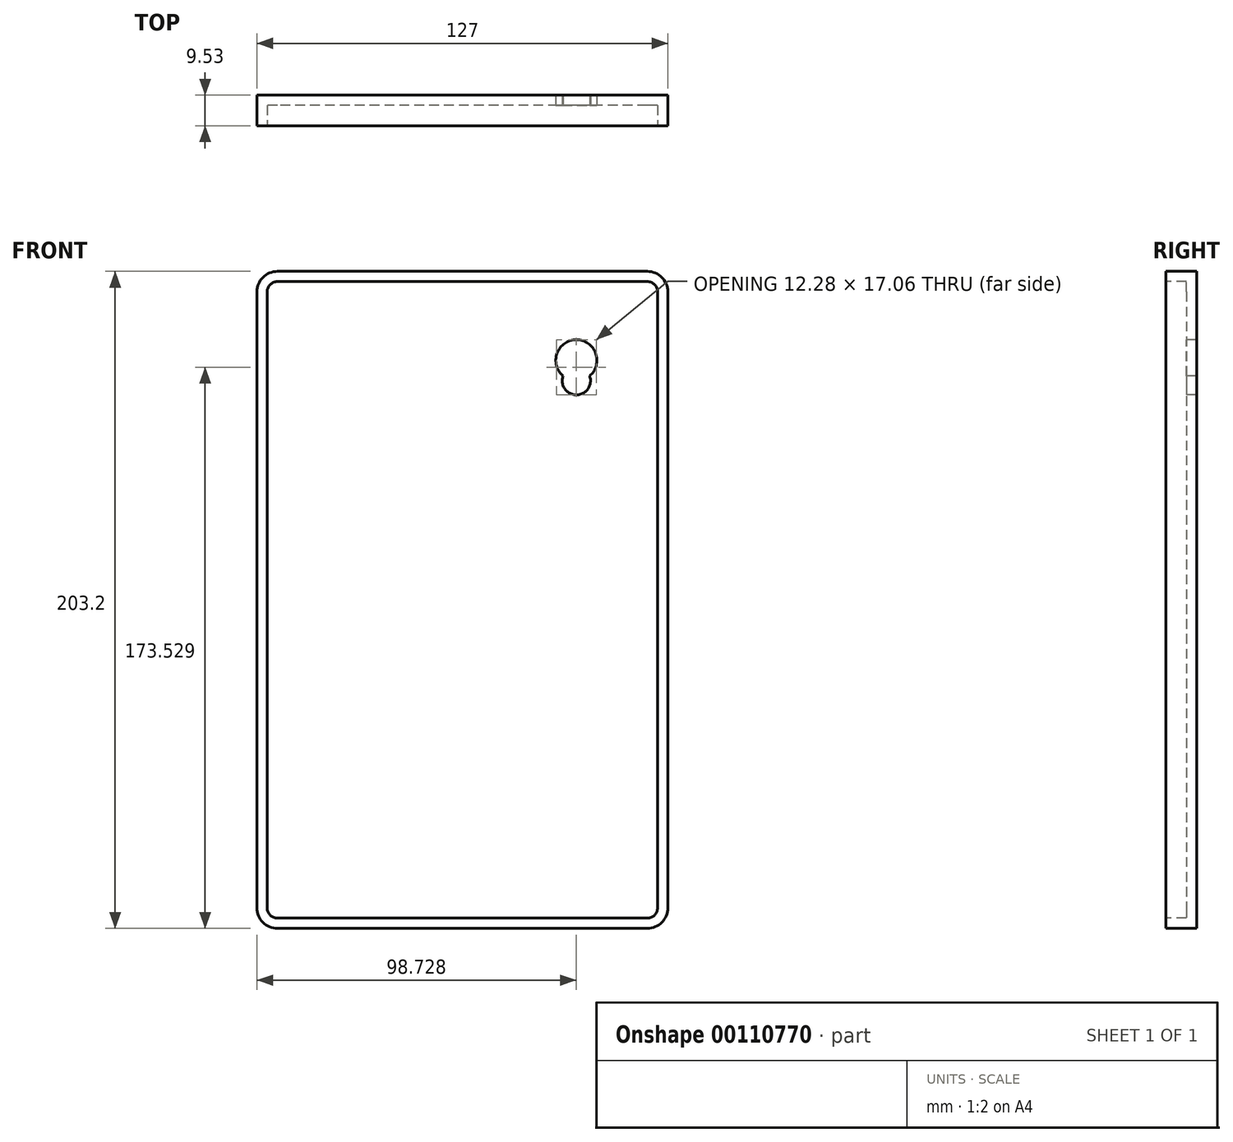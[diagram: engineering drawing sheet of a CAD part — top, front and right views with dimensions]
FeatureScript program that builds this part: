
annotation { "Feature Type Name" : "Feature", "Feature Type Description" : "" }
export const myFeature = defineFeature(function(context is Context, id is Id, definition is map)
    precondition{}
    {
        {
            var Q0;
            Q0=qCreatedBy(makeId("Front.planeOp"),FACE);
            var sketch = newSketch(context, id + "F0", { "sketchPlane" : qUnion([Q0])});
            skLineSegment(sketch, "E0.bottom", {"start": v(57.15, 101.6) * mm, "end": v(-57.15, 101.6) * mm});
            skLineSegment(sketch, "E0.top", {"start": v(57.15, -101.6) * mm, "end": v(-57.15, -101.6) * mm});
            skLineSegment(sketch, "E0.left", {"start": v(63.5, 95.25) * mm, "end": v(63.5, -95.25) * mm});
            skLineSegment(sketch, "E0.right", {"start": v(-63.5, 95.25) * mm, "end": v(-63.5, -95.25) * mm});
            skPoint(sketch, "E0.middle", {"position": v(0, 0) * mm});
            skPoint(sketch, "E1.visualSharp", {"position": v(-63.5, 101.6) * mm});
            skArc(sketch, "E1.filletArc", {"start": v(-57.15, 101.6) * mm, "mid": v(-61.64, 99.74) * mm, "end": v(-63.5, 95.25) * mm});
            skPoint(sketch, "E2.visualSharp", {"position": v(63.5, 101.6) * mm});
            skArc(sketch, "E2.filletArc", {"start": v(63.5, 95.25) * mm, "mid": v(61.64, 99.74) * mm, "end": v(57.15, 101.6) * mm});
            skPoint(sketch, "E3.visualSharp", {"position": v(63.5, -101.6) * mm});
            skArc(sketch, "E3.filletArc", {"start": v(57.15, -101.6) * mm, "mid": v(61.64, -99.74) * mm, "end": v(63.5, -95.25) * mm});
            skPoint(sketch, "E4.visualSharp", {"position": v(-63.5, -101.6) * mm});
            skArc(sketch, "E4.filletArc", {"start": v(-63.5, -95.25) * mm, "mid": v(-61.64, -99.74) * mm, "end": v(-57.15, -101.6) * mm});
            skSolve(sketch);
        }
        {
            var Q0;
            Q0=makeQuery(id+"F0.imprint","IMPRINT",FACE,{"disambiguationData":[TD([[makeQuery(id+"F0.imprint","IMPRINT",EDGE,{"derivedFrom":sQuery(id+"F0.wireOp",EDGE,"E0.bottom")}),1.0]])]});
            var Q1;
            Q1=sQuery(id+"F0.wireOp",EDGE,"E0.bottom");
            var Q2;
            Q2=sQuery(id+"F0.wireOp",EDGE,"E1.filletArc");
            var Q3;
            Q3=sQuery(id+"F0.wireOp",EDGE,"E0.right");
            var Q4;
            Q4=sQuery(id+"F0.wireOp",EDGE,"E2.filletArc");
            var Q5;
            Q5=sQuery(id+"F0.wireOp",EDGE,"E0.left");
            var Q6;
            Q6=sQuery(id+"F0.wireOp",EDGE,"E3.filletArc");
            var Q7;
            Q7=sQuery(id+"F0.wireOp",EDGE,"E0.top");
            var Q8;
            Q8=sQuery(id+"F0.wireOp",EDGE,"E4.filletArc");
            extrude(context, id + "F1", {"entities" : qUnion([Q0]), "surfaceEntities" : qUnion([Q1, Q2, Q3, Q4, Q5, Q6, Q7, Q8]), "depth" : 9.52 * mm});
        }
        {
            var Q0;
            Q0=makeQuery(id+"F1.opExtrude","CAP_FACE",FACE,{"disambiguationData":[OSD([sQuery(id+"F0.wireOp",EDGE,"E0.bottom"),sQuery(id+"F0.wireOp",EDGE,"E0.top"),sQuery(id+"F0.wireOp",EDGE,"E0.left"),sQuery(id+"F0.wireOp",EDGE,"E0.right"),sQuery(id+"F0.wireOp",EDGE,"E1.filletArc"),sQuery(id+"F0.wireOp",EDGE,"E2.filletArc"),sQuery(id+"F0.wireOp",EDGE,"E3.filletArc"),sQuery(id+"F0.wireOp",EDGE,"E4.filletArc")])],"isStart":false});
            var sketch = newSketch(context, id + "F2", { "sketchPlane" : qUnion([Q0])});
            skLineSegment(sketch, "E5.bottom", {"start": v(57.15, 98.43) * mm, "end": v(-57.15, 98.43) * mm});
            skLineSegment(sketch, "E5.top", {"start": v(57.15, -98.43) * mm, "end": v(-57.15, -98.43) * mm});
            skLineSegment(sketch, "E5.left", {"start": v(60.32, 95.25) * mm, "end": v(60.32, -95.25) * mm});
            skLineSegment(sketch, "E5.right", {"start": v(-60.32, 95.25) * mm, "end": v(-60.32, -95.25) * mm});
            skPoint(sketch, "E5.middle", {"position": v(0, 0) * mm});
            skPoint(sketch, "E6.visualSharp", {"position": v(-60.32, 98.43) * mm});
            skArc(sketch, "E6.filletArc", {"start": v(-57.15, 98.43) * mm, "mid": v(-59.4, 97.5) * mm, "end": v(-60.32, 95.25) * mm});
            skPoint(sketch, "E7.visualSharp", {"position": v(60.32, 98.43) * mm});
            skArc(sketch, "E7.filletArc", {"start": v(60.32, 95.25) * mm, "mid": v(59.4, 97.5) * mm, "end": v(57.15, 98.43) * mm});
            skPoint(sketch, "E8.visualSharp", {"position": v(60.32, -98.43) * mm});
            skArc(sketch, "E8.filletArc", {"start": v(57.15, -98.43) * mm, "mid": v(59.4, -97.5) * mm, "end": v(60.32, -95.25) * mm});
            skPoint(sketch, "E9.visualSharp", {"position": v(-60.32, -98.43) * mm});
            skArc(sketch, "E9.filletArc", {"start": v(-60.32, -95.25) * mm, "mid": v(-59.4, -97.5) * mm, "end": v(-57.15, -98.43) * mm});
            skSolve(sketch);
        }
        {
            var Q0;
            Q0 = qSketchRegion(id + "F2", true);
            extrude(context, id + "F3", {"entities" : qUnion([Q0]), "operationType" : NewBodyOperationType.REMOVE, "oppositeDirection" : true, "depth" : 6.35 * mm});
        }
        {
            var Q0;
            Q0=makeQuery(id+"F3.boolean.opBoolean","COPY",FACE,{"derivedFrom":makeQuery(id+"F3.opExtrude","CAP_FACE",FACE,{"disambiguationData":[OSD([sQuery(id+"F2.wireOp",EDGE,"E5.bottom"),sQuery(id+"F2.wireOp",EDGE,"E5.top"),sQuery(id+"F2.wireOp",EDGE,"E5.left"),sQuery(id+"F2.wireOp",EDGE,"E5.right"),sQuery(id+"F2.wireOp",EDGE,"E6.filletArc"),sQuery(id+"F2.wireOp",EDGE,"E7.filletArc"),sQuery(id+"F2.wireOp",EDGE,"E8.filletArc"),sQuery(id+"F2.wireOp",EDGE,"E9.filletArc")])],"isStart":false})});
            var sketch = newSketch(context, id + "F4", { "sketchPlane" : qUnion([Q0])});
            skArc(sketch, "E10", {"start": v(39.33, 69.26) * mm, "mid": v(35.23, 80.46) * mm, "end": v(31.13, 69.26) * mm});
            skArc(sketch, "E11", {"start": v(31.13, 69.26) * mm, "mid": v(35.23, 63.4) * mm, "end": v(39.33, 69.26) * mm});
            skSolve(sketch);
        }
        {
            var Q0;
            Q0 = qSketchRegion(id + "F4", true);
            extrude(context, id + "F5", {"entities" : qUnion([Q0]), "operationType" : NewBodyOperationType.REMOVE, "endBound" : BoundingType.UP_TO_NEXT, "oppositeDirection" : true, "depth" : 25.4 * mm});
        }
    });
